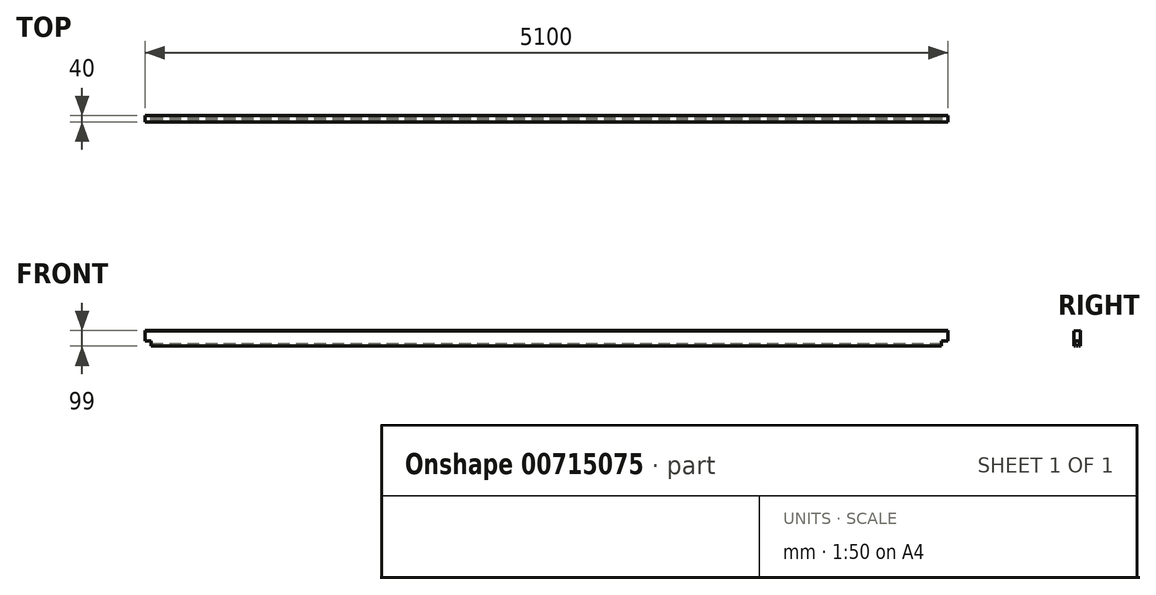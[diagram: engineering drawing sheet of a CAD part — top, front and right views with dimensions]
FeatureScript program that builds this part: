
annotation { "Feature Type Name" : "Feature", "Feature Type Description" : "" }
export const myFeature = defineFeature(function(context is Context, id is Id, definition is map)
    precondition{}
    {
        {
            var Q0;
            Q0=qCreatedBy(makeId("Right.planeOp"),FACE);
            var sketch = newSketch(context, id + "F0", { "sketchPlane" : qUnion([Q0])});
            skLineSegment(sketch, "E0", {"start": v(20, 56) * mm, "end": v(20, -70) * mm});
            skLineSegment(sketch, "E1", {"start": v(20, -70) * mm, "end": v(17, -73) * mm});
            skLineSegment(sketch, "E2", {"start": v(17, -73) * mm, "end": v(12, -73) * mm});
            skLineSegment(sketch, "E3", {"start": v(12, -59) * mm, "end": v(12, -73) * mm});
            skLineSegment(sketch, "E4", {"start": v(12, -59) * mm, "end": v(4, -59) * mm});
            skLineSegment(sketch, "E5", {"start": v(4, -73) * mm, "end": v(4, -59) * mm});
            skLineSegment(sketch, "E6", {"start": v(4, -73) * mm, "end": v(-4, -73) * mm});
            skLineSegment(sketch, "E7", {"start": v(-4, -59) * mm, "end": v(-4, -73) * mm});
            skLineSegment(sketch, "E8", {"start": v(-4, -59) * mm, "end": v(-12, -59) * mm});
            skLineSegment(sketch, "E9", {"start": v(-12, -73) * mm, "end": v(-12, -59) * mm});
            skLineSegment(sketch, "E10", {"start": v(-12, -73) * mm, "end": v(-17, -73) * mm});
            skLineSegment(sketch, "E11", {"start": v(-17, -73) * mm, "end": v(-20, -70) * mm});
            skLineSegment(sketch, "E12", {"start": v(-20, -70) * mm, "end": v(-20, 56) * mm});
            skLineSegment(sketch, "E13", {"start": v(-20, 56) * mm, "end": v(-17, 59) * mm});
            skLineSegment(sketch, "E14", {"start": v(-17, 59) * mm, "end": v(-12, 59) * mm});
            skLineSegment(sketch, "E15", {"start": v(-4, 59) * mm, "end": v(4, 59) * mm});
            skLineSegment(sketch, "E16", {"start": v(12, 59) * mm, "end": v(17, 59) * mm});
            skLineSegment(sketch, "E17", {"start": v(17, 59) * mm, "end": v(20, 56) * mm});
            skPoint(sketch, "E18.end.orphan", {"position": v(12, 57.8) * mm});
            skPoint(sketch, "E19.end.orphan", {"position": v(4, 66.3) * mm});
            skPoint(sketch, "E20.end.orphan", {"position": v(-4, 66.3) * mm});
            skLineSegment(sketch, "E21", {"start": v(-12, 59) * mm, "end": v(-12, 73) * mm});
            skLineSegment(sketch, "E22", {"start": v(-12, 73) * mm, "end": v(-4, 73) * mm});
            skLineSegment(sketch, "E23", {"start": v(-4, 73) * mm, "end": v(-4, 59) * mm});
            skLineSegment(sketch, "E24", {"start": v(4, 59) * mm, "end": v(4, 73) * mm});
            skLineSegment(sketch, "E25", {"start": v(4, 73) * mm, "end": v(12, 73) * mm});
            skLineSegment(sketch, "E26", {"start": v(12, 73) * mm, "end": v(12, 59) * mm});
            skSolve(sketch);
        }
        {
            var Q0;
            Q0=makeQuery(id+"F0.imprint","IMPRINT",FACE,{"disambiguationData":[TD([[makeQuery(id+"F0.imprint","IMPRINT",EDGE,{"derivedFrom":sQuery(id+"F0.wireOp",EDGE,"E0")}),-1.0]])]});
            extrude(context, id + "F1", {"entities" : qUnion([Q0]), "endBound" : BoundingType.SYMMETRIC, "depth" : 5100 * mm, "offsetDistance" : 25 * mm});
        }
        {
            var Q0;
            Q0=qCreatedBy(makeId("Front.planeOp"),FACE);
            var sketch = newSketch(context, id + "F2", { "sketchPlane" : qUnion([Q0])});
            skLineSegment(sketch, "E27.bottom", {"start": v(-2510, 92) * mm, "end": v(-2590, 92) * mm});
            skLineSegment(sketch, "E27.top", {"start": v(-2510, 26) * mm, "end": v(-2590, 26) * mm});
            skLineSegment(sketch, "E27.left", {"start": v(-2510, 92) * mm, "end": v(-2510, 26) * mm});
            skLineSegment(sketch, "E27.right", {"start": v(-2590, 92) * mm, "end": v(-2590, 26) * mm});
            skPoint(sketch, "E27.middle", {"position": v(-2550, 59) * mm});
            skLineSegment(sketch, "E28.bottom", {"start": v(-2510, -40) * mm, "end": v(-2590, -40) * mm});
            skLineSegment(sketch, "E28.top", {"start": v(-2510, -106) * mm, "end": v(-2590, -106) * mm});
            skLineSegment(sketch, "E28.left", {"start": v(-2510, -40) * mm, "end": v(-2510, -106) * mm});
            skLineSegment(sketch, "E28.right", {"start": v(-2590, -40) * mm, "end": v(-2590, -106) * mm});
            skPoint(sketch, "E28.middle", {"position": v(-2550, -73) * mm});
            skLineSegment(sketch, "E29.bottom", {"start": v(2510, 92) * mm, "end": v(2590, 92) * mm});
            skLineSegment(sketch, "E29.top", {"start": v(2510, 26) * mm, "end": v(2590, 26) * mm});
            skLineSegment(sketch, "E29.left", {"start": v(2510, 92) * mm, "end": v(2510, 26) * mm});
            skLineSegment(sketch, "E29.right", {"start": v(2590, 92) * mm, "end": v(2590, 26) * mm});
            skPoint(sketch, "E29.middle", {"position": v(2550, 59) * mm});
            skLineSegment(sketch, "E30.bottom", {"start": v(2510, -106) * mm, "end": v(2590, -106) * mm});
            skLineSegment(sketch, "E30.top", {"start": v(2510, -40) * mm, "end": v(2590, -40) * mm});
            skLineSegment(sketch, "E30.left", {"start": v(2510, -106) * mm, "end": v(2510, -40) * mm});
            skLineSegment(sketch, "E30.right", {"start": v(2590, -106) * mm, "end": v(2590, -40) * mm});
            skPoint(sketch, "E30.middle", {"position": v(2550, -73) * mm});
            skSolve(sketch);
        }
        {
            var Q0;
            Q0=makeQuery(id+"F2.imprint","IMPRINT",FACE,{"disambiguationData":[TD([[makeQuery(id+"F2.imprint","IMPRINT",EDGE,{"derivedFrom":sQuery(id+"F2.wireOp",EDGE,"E27.bottom")}),1.0]])]});
            var Q1;
            Q1=makeQuery(id+"F2.imprint","IMPRINT",FACE,{"disambiguationData":[TD([[makeQuery(id+"F2.imprint","IMPRINT",EDGE,{"derivedFrom":sQuery(id+"F2.wireOp",EDGE,"E28.bottom")}),1.0]])]});
            var Q2;
            Q2=makeQuery(id+"F2.imprint","IMPRINT",FACE,{"disambiguationData":[TD([[makeQuery(id+"F2.imprint","IMPRINT",EDGE,{"derivedFrom":sQuery(id+"F2.wireOp",EDGE,"E29.bottom")}),-1.0]])]});
            var Q3;
            Q3=makeQuery(id+"F2.imprint","IMPRINT",FACE,{"disambiguationData":[TD([[makeQuery(id+"F2.imprint","IMPRINT",EDGE,{"derivedFrom":sQuery(id+"F2.wireOp",EDGE,"E30.bottom")}),1.0]])]});
            extrude(context, id + "F3", {"entities" : qUnion([Q0, Q1, Q2, Q3]), "operationType" : NewBodyOperationType.REMOVE, "endBound" : BoundingType.SYMMETRIC, "oppositeDirection" : true, "depth" : 100 * mm, "offsetDistance" : 25 * mm});
        }
        {
            var Q0;
            Q0=qCreatedBy(makeId("Right.planeOp"),FACE);
            var sketch = newSketch(context, id + "F4", { "sketchPlane" : qUnion([Q0])});
            skLineSegment(sketch, "E31.bottom", {"start": v(-20, -40) * mm, "end": v(20, -40) * mm});
            skLineSegment(sketch, "E31.top", {"start": v(-20, -73) * mm, "end": v(20, -73) * mm});
            skLineSegment(sketch, "E31.left", {"start": v(-20, -40) * mm, "end": v(-20, -73) * mm});
            skLineSegment(sketch, "E31.right", {"start": v(20, -40) * mm, "end": v(20, -73) * mm});
            skSolve(sketch);
        }
        {
            var Q0;
            Q0=qCreatedBy(makeId("Right.planeOp"),FACE);
            var sketch = newSketch(context, id + "F5", { "sketchPlane" : qUnion([Q0])});
            skLineSegment(sketch, "E32", {"start": v(-30, 21.32) * mm, "end": v(30, 26.94) * mm});
            skLineSegment(sketch, "E33", {"start": v(30, 26.94) * mm, "end": v(30, 83) * mm});
            skLineSegment(sketch, "E34", {"start": v(30, 83) * mm, "end": v(-30, 83) * mm});
            skLineSegment(sketch, "E35", {"start": v(-30, 83) * mm, "end": v(-30, 21.32) * mm});
            skSolve(sketch);
        }
        {
            var Q0;
            Q0=makeQuery(id+"F5.imprint","IMPRINT",FACE,{"disambiguationData":[TD([[makeQuery(id+"F5.imprint","IMPRINT",EDGE,{"derivedFrom":sQuery(id+"F5.wireOp",EDGE,"E32")}),1.0]])]});
            extrude(context, id + "F6", {"entities" : qUnion([Q0]), "operationType" : NewBodyOperationType.REMOVE, "endBound" : BoundingType.THROUGH_ALL, "depth" : 25 * mm, "offsetDistance" : 25 * mm, "hasSecondDirection" : true, "secondDirectionBound" : SecondDirectionBoundingType.THROUGH_ALL, "secondDirectionOppositeDirection" : true, "secondDirectionDepth" : 25 * mm});
        }
    });
